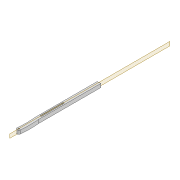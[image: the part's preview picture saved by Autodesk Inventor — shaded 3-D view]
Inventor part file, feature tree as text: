
AUTODESK INVENTOR PART (.ipt)
format: ipt  version: 2022 (Build 260153000, 153)  size: 126,464 bytes
history: native  units: mm
features: sketch x3, extrude x2, projected_geometry x1
ambient origin geometry x8: Origin, YZ Plane, XZ Plane, XY Plane, X Axis, Y Axis, Z Axis, Center Point
bodies: Solid1 (feature_tree)
feature tree (6):
  extrude  "Extrusion1"  Depth=8.0mm
  sketch  "Sketch2"  dims[d2=3.0mm d3=3.0mm]
  extrude  "Extrusion2"  Depth=3.0mm
  sketch  "Sketch1"  dims[d0=319.927mm d1=8.0mm]
  projected_geometry  "Projected Loop1"
  sketch  "Sketch3"  dims[d4=8.0mm d5=0.0mm d12=3.0mm d13=50.8mm d14=100.0mm d15=40.0mm d16=200.0mm d17=200.0mm d18=20.0mm d19=0.0mm d20=0.5mm d21=0.872665mm]
